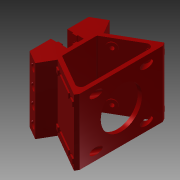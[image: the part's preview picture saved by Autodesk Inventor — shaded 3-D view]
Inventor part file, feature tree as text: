
AUTODESK INVENTOR PART (.ipt)
format: ipt  version: 2015 SP1 (Build 190203100, 203)  size: 562,688 bytes
history: native  units: mm
features: sketch x15, extrude x11, plane x4, hole x4, fillet x2
ambient origin geometry x8: Origin, YZ Plane, XZ Plane, XY Plane, X Axis, Y Axis, Z Axis, Center Point
bodies: Solid2 (feature_tree)
feature tree (36):
  extrude  "Extrusion13"  Depth=54.0mm
  fillet  "Fillet5"  Radius=20.0mm
  extrude  "Extrusion2"  Depth=2.0mm
  extrude  "Extrusion7"  Depth=2.0mm
  plane  "Work Plane20"
  hole  "Hole2"  [1 undecoded]
  plane  "Work Plane21"
  hole  "Hole3"  [1 undecoded]
  plane  "Work Plane18"
  hole  "Hole7"  [1 undecoded]
  plane  "Work Plane19"
  hole  "Hole8"  [1 undecoded]
  extrude  "Extrusion14"  Depth=5.5mm
  extrude  "Extrusion15"  Depth=5.5mm
  fillet  "Fillet6"  Radius=3.0mm
  extrude  "Extrusion16"  TaperAngle=60.0deg  [1 undecoded]
  extrude  "Extrusion17"  TaperAngle=60.0deg  [1 undecoded]
  extrude  "Extrusion18"  Depth=20.0mm
  extrude  "Extrusion19"  Depth=20.0mm
  extrude  "Extrusion20"  Depth=6.25mm
  extrude  "Extrusion21"  Depth=20.0mm
  sketch  "Sketch1"  dims[d11=20.0mm d12=54.0mm d19=20.0mm]
  sketch  "Sketch2"  dims[d23=6.0mm d24=2.0mm]
  sketch  "Sketch8"  dims[d25=6.0mm d26=2.0mm]
  sketch  "Sketch9"  dims[d27=60.0mm d28=0.0mm d63=8.0mm d64=0.0mm]
  sketch  "Sketch10"  dims[d65=4.5mm d66=6.0mm d67=8.0mm d68=32.0mm d69=90.0deg d70=30.0mm d71=20.594885mm d73=35.0mm]
  sketch  "Sketch20"  dims[d74=35.0mm]
  sketch  "Sketch21"  dims[d78=4.5mm d79=6.0mm d80=8.0mm d81=32.0mm d82=90.0deg d83=8.0mm d84=20.594885mm d110=42.5mm]
  sketch  "Sketch22"  dims[d166=80.0mm d167=0.0mm d168=20.0mm]
  sketch  "Sketch23"  dims[d169=20.0mm d171=5.5mm]
  sketch  "Sketch24"  dims[d172=3.0mm d173=5.5mm d174=3.0mm]
  sketch  "Sketch26"  dims[d176=5.0mm d177=60.0deg]
  sketch  "Sketch27"  dims[d178=120.0deg d179=60.0deg]
  sketch  "Sketch28"  dims[d181=20.0mm d184=1.5mm]
  sketch  "Sketch29"  dims[d185=5.5mm d186=20.0mm]
  sketch  "Sketch30"  dims[d188=4.5mm d189=6.0mm d190=8.0mm d191=16.35mm d192=90.0deg d193=8.0mm d194=20.594885mm d195=35.214053mm d196=20.0mm d197=4.5mm d198=6.0mm d199=8.0mm d200=16.35mm d201=90.0deg d202=8.0mm d203=20.594885mm d204=33.0mm d205=10.0mm d206=5.0mm d207=33.0mm d208=10.0mm d209=54.0mm d210=20.0mm d211=20.0mm d212=20.0mm d213=20.0mm d214=20.0mm d215=50.0mm d216=10.0mm d217=0.0mm d218=15.0mm d219=10.0mm d220=0.0mm d221=2.0mm d222=12.0mm d223=12.0mm d224=1.0mm d225=0.0mm d228=12.0mm d229=12.0mm d230=12.0mm d231=12.0mm d232=12.0mm d233=12.0mm d234=1.0mm d235=0.0mm d236=6.25mm d237=6.25mm d238=6.25mm d239=6.25mm d240=6.25mm d241=6.25mm d242=6.25mm d243=6.25mm d244=1.0mm d245=0.0mm d246=6.25mm d247=6.25mm d248=6.25mm d249=6.25mm d250=6.25mm d251=6.25mm d252=6.25mm d253=6.25mm d254=1.0mm d255=0.0mm d256=6.25mm d257=6.25mm d258=6.25mm d259=6.25mm d260=6.25mm d261=6.25mm d262=6.25mm d263=6.25mm d264=1.0mm d265=0.0mm d266=6.25mm d267=6.25mm d268=6.25mm d269=6.25mm d270=6.25mm d271=6.25mm d272=6.25mm d273=6.25mm d274=1.0mm d275=0.0mm]
note: 6 required parameter values undecoded (feature->parameter linkage not recoverable at this tier; creation-order binding heuristic only, values carry confidence <= 0.55)
